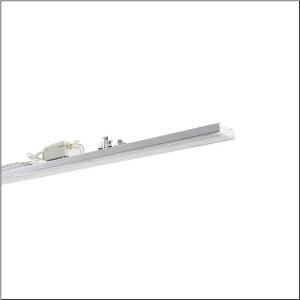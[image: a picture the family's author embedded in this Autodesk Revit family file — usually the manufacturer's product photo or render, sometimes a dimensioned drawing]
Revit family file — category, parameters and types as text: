
# Revit family: licross_21_recessed_ho_52tl1edn4e5s
name_source: partatom
category: Lighting Fixtures
units: mm (PartAtom-declared; Revit-internal decimal feet)

## family parameters
Cut with Voids When Loaded = No
Host = Face
Light Source = No
Part Type = Normal
Room Calculation Point = No
Round Connector Dimension = Use Diameter
Shared = No

## types (1)
- --- (1 x LED, 14620 lm, 84.6 W, 4000K)
    Apparent Load = 85 VA
    CIE Flux Codes = 85 95 99 100 100
    Color Rendering = 80
    Color Temperature = 4000K
    Default Elevation = 1800 mm
    Description = Licross 21 Recessed HO, luminaire insert, of sheet steel, galvanised, coil coated, white, length: 1.500mm, width: 66mm, height: 67mm, LED rated luminous flux: 14.620lm, light colour: 840, SDCM (Standard Deviation of Colour Matching)MacAdam ≤ 3 SDCM (initial), control gear: DALI 2, with plug, 5-pole, with phase selection, mains connection: 220..240V, AC, 50/60Hz, rated input power: 85W, internal wiring halogen-free, primary light control with lens, of plastic, primary optical cover: cover, of PMMA, light emission: direct distribution, primary light characteristic: symmetric, protection rating (complete): IP40, insulation class (complete): insulation class I (protective earthing), certification: CE, ENEC, VDE, UKCA, protection symbol: D if used in an environment without relevant dust loads with corresponding accessories, impact resistance: IK06, permissible ambient temperature for indoor applications: -25..+30°C, corresponds to IFS (International Featured Standards) requirements for safety and quality in the food industry, reducing of maximum allowable ambient temperature of 5°C with ceiling mounting, LABS conformity tested according to VDMA 24364:2018-05, The light source and the operating device comply with the requirements of the Ecodesign Regulation (EU) 2019/2020 and are replaceable in accordance with this regulation, packaging unit: 1 piece
    Height = 58 mm
    Lamp = 1 x LED
    Lamp Light Flux = 14620 lm
    Lamp Power = 84.6 W
    Lamp count = 1
    Length = 1500 mm
    Luminous efficacy = 173 lm/W
    Manufacturer = Siteco
    ModVariant = No
    Model = 52TL1EDN4E5S
    Mounting Place = Ceiling
    Mounting Type = Pendant
    Number of Poles = 1
    OnlyDefault = Yes
    Power Factor = 1
    Product Name = Licross 21 Recessed HO
    Product group = luminaire insert | ceiling pendant
    ProductGroupID = 901
    Protection Class = Protection class I
    Protection Degree = IP 40
    RLX_Detail_Level = 1
    RLX_Emergency_Light_Flux = 0 lm
    RLX_Emergency_Type = 0
    RLX_Emergency_Type_DB = No
    RlxData = <blob elided: 25041 chars, md5=c3b4513b>
    Socket = socket
    Standby Power = 0 W
    System Light Flux = 14620 lm
    System Power = 85 W
    Type Comments = factory setting: luminous flux: 100 % | dim-lin: 254 | 484 mA
    Type Image = l_1296930.jpg
    URL = http://relux.com
    VarID = @adj_126901
    Voltage = 0 V
    Weight = 0.00 kg
    Width = 66 mm

## geometry (parser evidence)
native form markers: Blend x4, Sweep x11
no freeform markers — native parametric forms only
